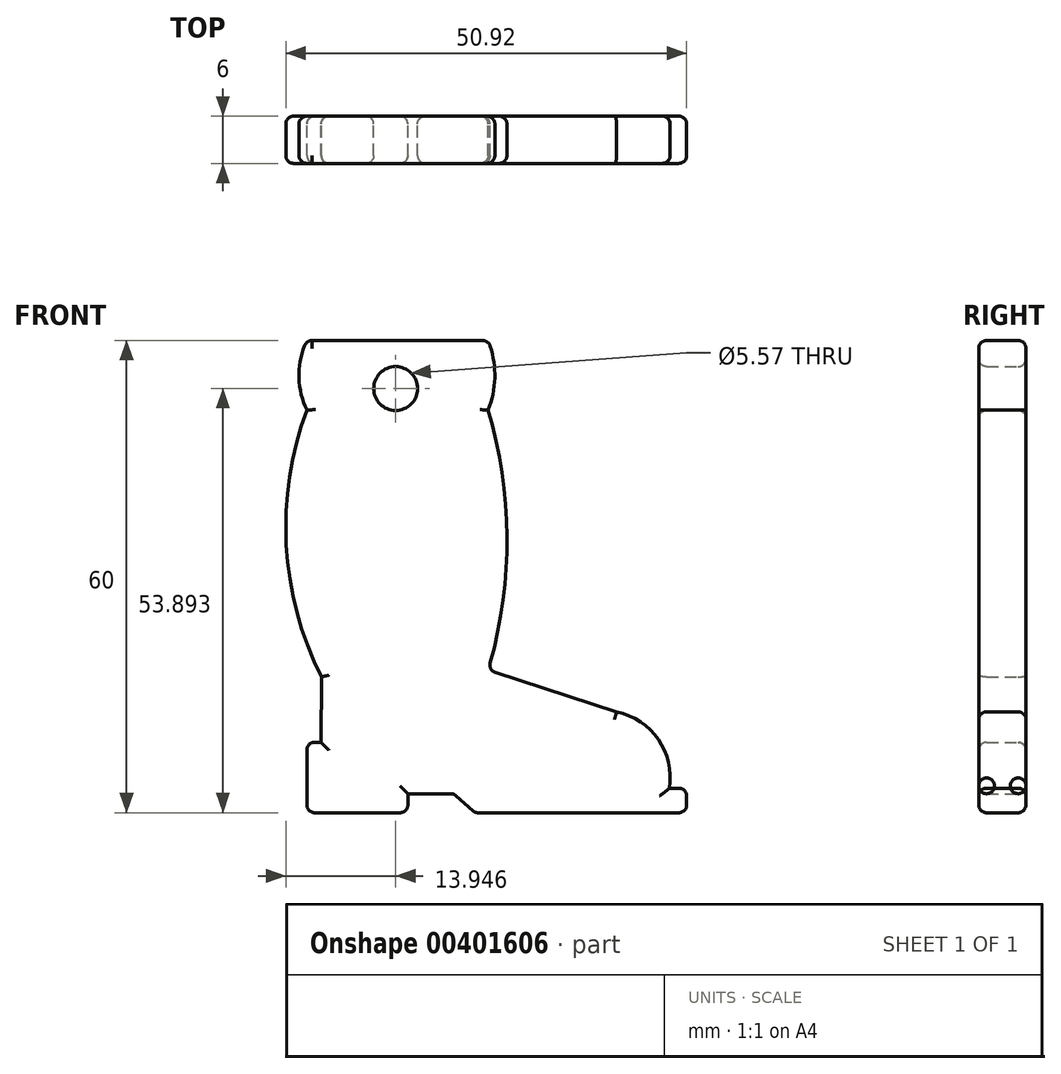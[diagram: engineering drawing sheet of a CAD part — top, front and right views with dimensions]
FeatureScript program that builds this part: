
annotation { "Feature Type Name" : "Feature", "Feature Type Description" : "" }
export const myFeature = defineFeature(function(context is Context, id is Id, definition is map)
    precondition{}
    {
        {
            var Q0;
            Q0=qCreatedBy(makeId("Front.planeOp"),FACE);
            var sketch = newSketch(context, id + "F0", { "sketchPlane" : qUnion([Q0])});
            skLineSegment(sketch, "E0", {"start": v(0, 0) * mm, "end": v(0, 8.95) * mm});
            skLineSegment(sketch, "E1", {"start": v(0, 0) * mm, "end": v(12.82, 0) * mm});
            skLineSegment(sketch, "E2", {"start": v(12.82, 0) * mm, "end": v(12.82, 2.42) * mm});
            skLineSegment(sketch, "E3", {"start": v(12.82, 2.42) * mm, "end": v(18.66, 2.42) * mm});
            skLineSegment(sketch, "E4", {"start": v(18.66, 2.42) * mm, "end": v(21.36, 0) * mm});
            skLineSegment(sketch, "E5", {"start": v(21.36, 0) * mm, "end": v(48.24, 0) * mm});
            skLineSegment(sketch, "E6", {"start": v(48.24, 0) * mm, "end": v(48.24, 3.12) * mm});
            skLineSegment(sketch, "E7", {"start": v(48.24, 3.12) * mm, "end": v(46.04, 3.12) * mm});
            skArc(sketch, "E8", {"start": v(46.04, 3.12) * mm, "mid": v(44.64, 9.32) * mm, "end": v(39.34, 12.82) * mm});
            skLineSegment(sketch, "E9", {"start": v(39.34, 12.82) * mm, "end": v(23.02, 18.1) * mm});
            skArc(sketch, "E10", {"start": v(23.02, 18.1) * mm, "mid": v(25.41, 34.63) * mm, "end": v(23.02, 51.16) * mm});
            skArc(sketch, "E11", {"start": v(23.02, 51.16) * mm, "mid": v(23.87, 55.58) * mm, "end": v(23.02, 60) * mm});
            skLineSegment(sketch, "E12", {"start": v(23.02, 60) * mm, "end": v(0, 60) * mm});
            skArc(sketch, "E13", {"start": v(0, 60) * mm, "mid": v(-1.02, 55.58) * mm, "end": v(0, 51.16) * mm});
            skArc(sketch, "E14", {"start": v(0, 51.16) * mm, "mid": v(-2.62, 34.02) * mm, "end": v(1.84, 17.26) * mm});
            skLineSegment(sketch, "E15", {"start": v(0, 8.95) * mm, "end": v(1.8, 8.95) * mm});
            skLineSegment(sketch, "E16", {"start": v(1.8, 8.95) * mm, "end": v(1.84, 17.26) * mm});
            skCircle(sketch, "E17", {"center": v(11.27, 53.9) * mm, "radius": 2.78 * mm});
            skSolve(sketch);
        }
        {
            var Q0;
            Q0=makeQuery(id+"F0.imprint","IMPRINT",FACE,{"disambiguationData":[TD([[makeQuery(id+"F0.imprint","IMPRINT",EDGE,{"derivedFrom":sQuery(id+"F0.wireOp",EDGE,"E0")}),-1.0]])]});
            extrude(context, id + "F1", {"entities" : qUnion([Q0]), "endBound" : BoundingType.SYMMETRIC, "depth" : 6 * mm});
        }
        {
            var Q0;
            Q0=makeQuery(id+"F1.opExtrude","SWEPT_EDGE",EDGE,{"disambiguationData":[OSD([sQuery(id+"F0.wireOp",EDGE,"E11"),sQuery(id+"F0.wireOp",EDGE,"E12")])]});
            var Q1;
            Q1=makeQuery(id+"F1.opExtrude","SWEPT_EDGE",EDGE,{"disambiguationData":[OSD([sQuery(id+"F0.wireOp",EDGE,"E12"),sQuery(id+"F0.wireOp",EDGE,"E13")])]});
            var Q2;
            Q2=makeQuery(id+"F1.opExtrude","SWEPT_EDGE",EDGE,{"disambiguationData":[OSD([sQuery(id+"F0.wireOp",EDGE,"E3"),sQuery(id+"F0.wireOp",EDGE,"E4")])]});
            var Q3;
            Q3=makeQuery(id+"F1.opExtrude","SWEPT_EDGE",EDGE,{"disambiguationData":[OSD([sQuery(id+"F0.wireOp",EDGE,"E4"),sQuery(id+"F0.wireOp",EDGE,"E5")])]});
            var Q4;
            Q4=makeQuery(id+"F1.opExtrude","SWEPT_EDGE",EDGE,{"disambiguationData":[OSD([sQuery(id+"F0.wireOp",EDGE,"E5"),sQuery(id+"F0.wireOp",EDGE,"E6")])]});
            var Q5;
            Q5=makeQuery(id+"F1.opExtrude","SWEPT_EDGE",EDGE,{"disambiguationData":[OSD([sQuery(id+"F0.wireOp",EDGE,"E0"),sQuery(id+"F0.wireOp",EDGE,"E1")])]});
            var Q6;
            Q6=makeQuery(id+"F1.opExtrude","SWEPT_EDGE",EDGE,{"disambiguationData":[OSD([sQuery(id+"F0.wireOp",EDGE,"E0"),sQuery(id+"F0.wireOp",EDGE,"E15")])]});
            var Q7;
            Q7=makeQuery(id+"F1.opExtrude","SWEPT_EDGE",EDGE,{"disambiguationData":[OSD([sQuery(id+"F0.wireOp",EDGE,"E6"),sQuery(id+"F0.wireOp",EDGE,"E7")])]});
            var Q8;
            Q8=makeQuery(id+"F1.opExtrude","SWEPT_EDGE",EDGE,{"disambiguationData":[OSD([sQuery(id+"F0.wireOp",EDGE,"E1"),sQuery(id+"F0.wireOp",EDGE,"E2")])]});
            var Q9;
            Q9=makeQuery(id+"F1.opExtrude","SWEPT_EDGE",EDGE,{"disambiguationData":[OSD([sQuery(id+"F0.wireOp",EDGE,"E9"),sQuery(id+"F0.wireOp",EDGE,"E10")])]});
            var Q10;
            Q10=makeQuery(id+"F1.opExtrude","CAP_FACE",FACE,{"disambiguationData":[OSD([sQuery(id+"F0.wireOp",EDGE,"E0"),sQuery(id+"F0.wireOp",EDGE,"E1"),sQuery(id+"F0.wireOp",EDGE,"E2"),sQuery(id+"F0.wireOp",EDGE,"E3"),sQuery(id+"F0.wireOp",EDGE,"E4"),sQuery(id+"F0.wireOp",EDGE,"E5"),sQuery(id+"F0.wireOp",EDGE,"E6"),sQuery(id+"F0.wireOp",EDGE,"E7"),sQuery(id+"F0.wireOp",EDGE,"E8"),sQuery(id+"F0.wireOp",EDGE,"E9"),sQuery(id+"F0.wireOp",EDGE,"E10"),sQuery(id+"F0.wireOp",EDGE,"E11"),sQuery(id+"F0.wireOp",EDGE,"E12"),sQuery(id+"F0.wireOp",EDGE,"E13"),sQuery(id+"F0.wireOp",EDGE,"E14"),sQuery(id+"F0.wireOp",EDGE,"E15"),sQuery(id+"F0.wireOp",EDGE,"E16"),sQuery(id+"F0.wireOp",EDGE,"E17")])],"isStart":false});
            var Q11;
            Q11=makeQuery(id+"F1.opExtrude","CAP_FACE",FACE,{"disambiguationData":[OSD([sQuery(id+"F0.wireOp",EDGE,"E0"),sQuery(id+"F0.wireOp",EDGE,"E1"),sQuery(id+"F0.wireOp",EDGE,"E2"),sQuery(id+"F0.wireOp",EDGE,"E3"),sQuery(id+"F0.wireOp",EDGE,"E4"),sQuery(id+"F0.wireOp",EDGE,"E5"),sQuery(id+"F0.wireOp",EDGE,"E6"),sQuery(id+"F0.wireOp",EDGE,"E7"),sQuery(id+"F0.wireOp",EDGE,"E8"),sQuery(id+"F0.wireOp",EDGE,"E9"),sQuery(id+"F0.wireOp",EDGE,"E10"),sQuery(id+"F0.wireOp",EDGE,"E11"),sQuery(id+"F0.wireOp",EDGE,"E12"),sQuery(id+"F0.wireOp",EDGE,"E13"),sQuery(id+"F0.wireOp",EDGE,"E14"),sQuery(id+"F0.wireOp",EDGE,"E15"),sQuery(id+"F0.wireOp",EDGE,"E16"),sQuery(id+"F0.wireOp",EDGE,"E17")])],"isStart":true});
            fillet(context, id + "F2", {"entities" : qUnion([Q0, Q1, Q2, Q3, Q4, Q5, Q6, Q7, Q8, Q9, Q10, Q11]), "radius" : 1 * mm, "tangentPropagation" : true, "allowEdgeOverflow" : false});
        }
    });
